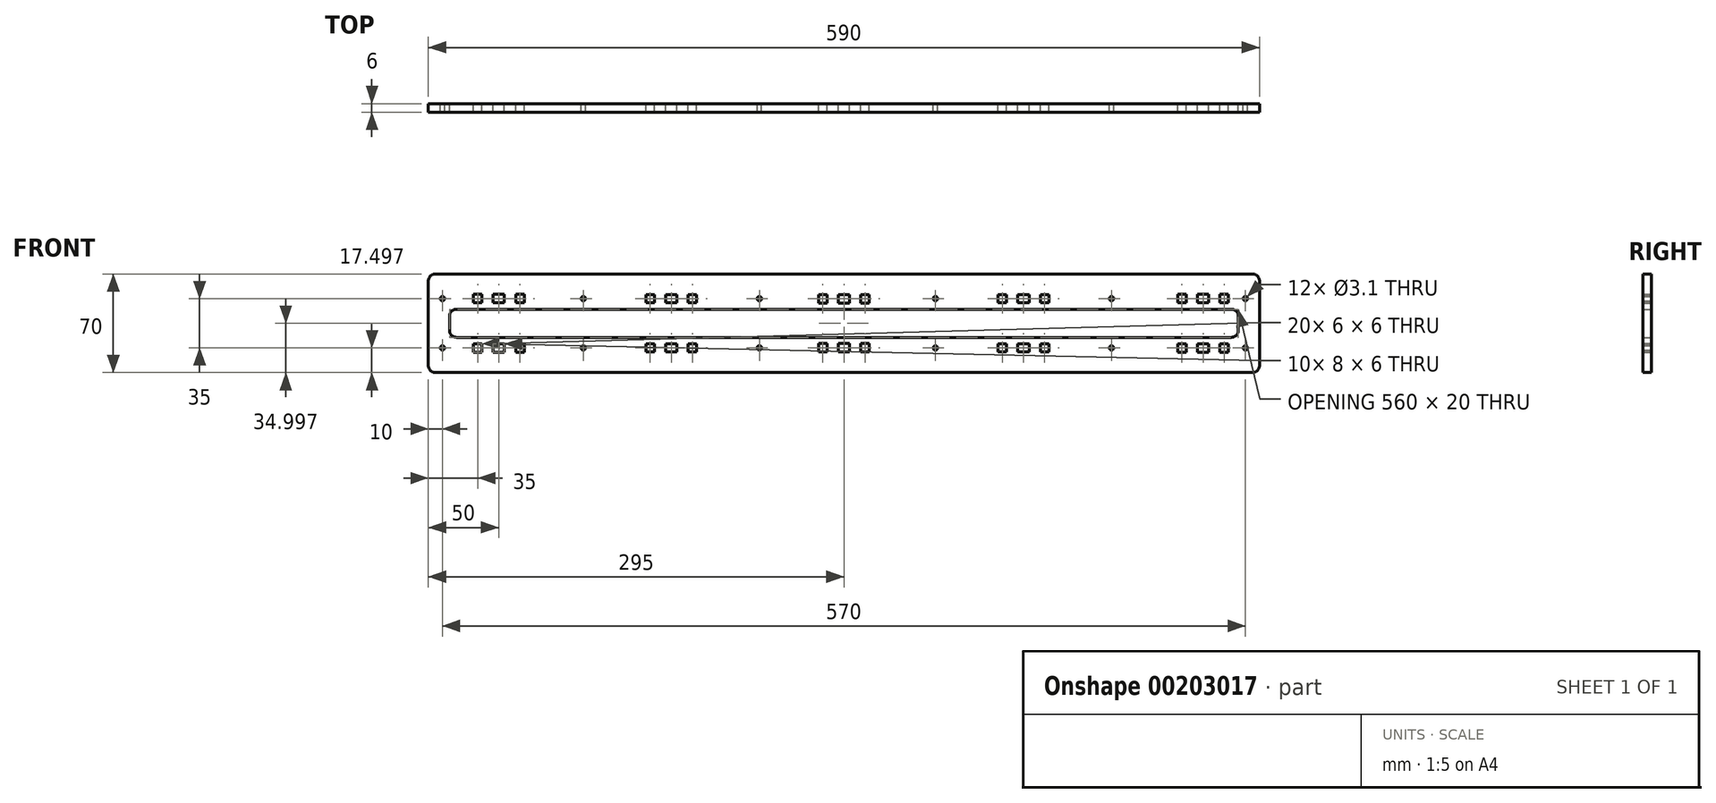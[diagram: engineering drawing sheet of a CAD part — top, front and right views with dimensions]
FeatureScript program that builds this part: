
annotation { "Feature Type Name" : "Feature", "Feature Type Description" : "" }
export const myFeature = defineFeature(function(context is Context, id is Id, definition is map)
    precondition{}
    {
        {
            var Q0;
            Q0=qCreatedBy(makeId("Front.planeOp"),FACE);
            var sketch = newSketch(context, id + "F0", { "sketchPlane" : qUnion([Q0])});
            skLineSegment(sketch, "E0", {"start": v(-295, -83) * mm, "end": v(-295, -23) * mm});
            skArc(sketch, "E1", {"start": v(-295, -23) * mm, "mid": v(-293.54, -19.47) * mm, "end": v(-290, -18) * mm});
            skLineSegment(sketch, "E2", {"start": v(-290, -18) * mm, "end": v(290, -18) * mm});
            skArc(sketch, "E3", {"start": v(290, -18) * mm, "mid": v(293.54, -19.47) * mm, "end": v(295, -23) * mm});
            skLineSegment(sketch, "E4", {"start": v(295, -23) * mm, "end": v(295, -83) * mm});
            skArc(sketch, "E5", {"start": v(295, -83) * mm, "mid": v(293.54, -86.54) * mm, "end": v(290, -88) * mm});
            skLineSegment(sketch, "E6", {"start": v(290, -88) * mm, "end": v(-290, -88) * mm});
            skArc(sketch, "E7", {"start": v(-290, -88) * mm, "mid": v(-293.54, -86.54) * mm, "end": v(-295, -83) * mm});
            skCircle(sketch, "E8", {"center": v(-285, -70.5) * mm, "radius": 1.55 * mm});
            skCircle(sketch, "E9", {"center": v(-285, -35.5) * mm, "radius": 1.55 * mm});
            skCircle(sketch, "E10", {"center": v(285, -70.5) * mm, "radius": 1.55 * mm});
            skCircle(sketch, "E11", {"center": v(285, -35.5) * mm, "radius": 1.55 * mm});
            skLineSegment(sketch, "E12", {"start": v(-275, -43) * mm, "end": v(275, -43) * mm});
            skArc(sketch, "E13", {"start": v(275, -43) * mm, "mid": v(278.54, -44.47) * mm, "end": v(280, -48) * mm});
            skLineSegment(sketch, "E14", {"start": v(280, -48) * mm, "end": v(280, -58) * mm});
            skArc(sketch, "E15", {"start": v(280, -58) * mm, "mid": v(278.54, -61.54) * mm, "end": v(275, -63) * mm});
            skLineSegment(sketch, "E16", {"start": v(275, -63) * mm, "end": v(-275, -63) * mm});
            skArc(sketch, "E17", {"start": v(-275, -63) * mm, "mid": v(-278.54, -61.54) * mm, "end": v(-280, -58) * mm});
            skLineSegment(sketch, "E18", {"start": v(-280, -58) * mm, "end": v(-280, -48) * mm});
            skArc(sketch, "E19", {"start": v(-280, -48) * mm, "mid": v(-278.54, -44.47) * mm, "end": v(-275, -43) * mm});
            skLineSegment(sketch, "E20", {"start": v(-249, -38.5) * mm, "end": v(-249, -32.5) * mm});
            skLineSegment(sketch, "E21", {"start": v(-249, -32.5) * mm, "end": v(-241, -32.5) * mm});
            skLineSegment(sketch, "E22", {"start": v(-241, -32.5) * mm, "end": v(-241, -38.5) * mm});
            skLineSegment(sketch, "E23", {"start": v(-241, -38.5) * mm, "end": v(-249, -38.5) * mm});
            skLineSegment(sketch, "E24", {"start": v(-233, -38.5) * mm, "end": v(-233, -32.5) * mm});
            skLineSegment(sketch, "E25", {"start": v(-233, -32.5) * mm, "end": v(-227, -32.5) * mm});
            skLineSegment(sketch, "E26", {"start": v(-227, -32.5) * mm, "end": v(-227, -38.5) * mm});
            skLineSegment(sketch, "E27", {"start": v(-227, -38.5) * mm, "end": v(-233, -38.5) * mm});
            skLineSegment(sketch, "E28", {"start": v(-257, -38.5) * mm, "end": v(-257, -32.5) * mm});
            skLineSegment(sketch, "E29", {"start": v(-257, -32.5) * mm, "end": v(-263, -32.5) * mm});
            skLineSegment(sketch, "E30", {"start": v(-263, -32.5) * mm, "end": v(-263, -38.5) * mm});
            skLineSegment(sketch, "E31", {"start": v(-263, -38.5) * mm, "end": v(-257, -38.5) * mm});
            skLineSegment(sketch, "E32", {"start": v(-126.5, -38.54) * mm, "end": v(-126.5, -32.54) * mm});
            skLineSegment(sketch, "E33", {"start": v(-126.5, -32.54) * mm, "end": v(-118.5, -32.54) * mm});
            skLineSegment(sketch, "E34", {"start": v(-118.5, -32.54) * mm, "end": v(-118.5, -38.54) * mm});
            skLineSegment(sketch, "E35", {"start": v(-118.5, -38.54) * mm, "end": v(-126.5, -38.54) * mm});
            skLineSegment(sketch, "E36", {"start": v(-110.5, -38.54) * mm, "end": v(-110.5, -32.54) * mm});
            skLineSegment(sketch, "E37", {"start": v(-110.5, -32.54) * mm, "end": v(-104.5, -32.54) * mm});
            skLineSegment(sketch, "E38", {"start": v(-104.5, -32.54) * mm, "end": v(-104.5, -38.54) * mm});
            skLineSegment(sketch, "E39", {"start": v(-104.5, -38.54) * mm, "end": v(-110.5, -38.54) * mm});
            skLineSegment(sketch, "E40", {"start": v(-134.5, -38.54) * mm, "end": v(-134.5, -32.54) * mm});
            skLineSegment(sketch, "E41", {"start": v(-134.5, -32.54) * mm, "end": v(-140.5, -32.54) * mm});
            skLineSegment(sketch, "E42", {"start": v(-140.5, -32.54) * mm, "end": v(-140.5, -38.54) * mm});
            skLineSegment(sketch, "E43", {"start": v(-140.5, -38.54) * mm, "end": v(-134.5, -38.54) * mm});
            skLineSegment(sketch, "E44", {"start": v(-4, -38.57) * mm, "end": v(-4, -32.57) * mm});
            skLineSegment(sketch, "E45", {"start": v(-4, -32.57) * mm, "end": v(4, -32.57) * mm});
            skLineSegment(sketch, "E46", {"start": v(4, -32.57) * mm, "end": v(4, -38.57) * mm});
            skLineSegment(sketch, "E47", {"start": v(4, -38.57) * mm, "end": v(-4, -38.57) * mm});
            skLineSegment(sketch, "E48", {"start": v(12, -38.57) * mm, "end": v(12, -32.57) * mm});
            skLineSegment(sketch, "E49", {"start": v(12, -32.57) * mm, "end": v(18, -32.57) * mm});
            skLineSegment(sketch, "E50", {"start": v(18, -32.57) * mm, "end": v(18, -38.57) * mm});
            skLineSegment(sketch, "E51", {"start": v(18, -38.57) * mm, "end": v(12, -38.57) * mm});
            skLineSegment(sketch, "E52", {"start": v(-12, -38.57) * mm, "end": v(-12, -32.57) * mm});
            skLineSegment(sketch, "E53", {"start": v(-12, -32.57) * mm, "end": v(-18, -32.57) * mm});
            skLineSegment(sketch, "E54", {"start": v(-18, -32.57) * mm, "end": v(-18, -38.57) * mm});
            skLineSegment(sketch, "E55", {"start": v(-18, -38.57) * mm, "end": v(-12, -38.57) * mm});
            skLineSegment(sketch, "E56", {"start": v(123.5, -38.54) * mm, "end": v(123.5, -32.54) * mm});
            skLineSegment(sketch, "E57", {"start": v(123.5, -32.54) * mm, "end": v(131.5, -32.54) * mm});
            skLineSegment(sketch, "E58", {"start": v(131.5, -32.54) * mm, "end": v(131.5, -38.54) * mm});
            skLineSegment(sketch, "E59", {"start": v(131.5, -38.54) * mm, "end": v(123.5, -38.54) * mm});
            skLineSegment(sketch, "E60", {"start": v(139.5, -38.54) * mm, "end": v(139.5, -32.54) * mm});
            skLineSegment(sketch, "E61", {"start": v(139.5, -32.54) * mm, "end": v(145.5, -32.54) * mm});
            skLineSegment(sketch, "E62", {"start": v(145.5, -32.54) * mm, "end": v(145.5, -38.54) * mm});
            skLineSegment(sketch, "E63", {"start": v(145.5, -38.54) * mm, "end": v(139.5, -38.54) * mm});
            skLineSegment(sketch, "E64", {"start": v(115.5, -38.54) * mm, "end": v(115.5, -32.54) * mm});
            skLineSegment(sketch, "E65", {"start": v(115.5, -32.54) * mm, "end": v(109.5, -32.54) * mm});
            skLineSegment(sketch, "E66", {"start": v(109.5, -32.54) * mm, "end": v(109.5, -38.54) * mm});
            skLineSegment(sketch, "E67", {"start": v(109.5, -38.54) * mm, "end": v(115.5, -38.54) * mm});
            skLineSegment(sketch, "E68", {"start": v(251, -38.5) * mm, "end": v(251, -32.5) * mm});
            skLineSegment(sketch, "E69", {"start": v(251, -32.5) * mm, "end": v(259, -32.5) * mm});
            skLineSegment(sketch, "E70", {"start": v(259, -32.5) * mm, "end": v(259, -38.5) * mm});
            skLineSegment(sketch, "E71", {"start": v(259, -38.5) * mm, "end": v(251, -38.5) * mm});
            skLineSegment(sketch, "E72", {"start": v(267, -38.5) * mm, "end": v(267, -32.5) * mm});
            skLineSegment(sketch, "E73", {"start": v(267, -32.5) * mm, "end": v(273, -32.5) * mm});
            skLineSegment(sketch, "E74", {"start": v(273, -32.5) * mm, "end": v(273, -38.5) * mm});
            skLineSegment(sketch, "E75", {"start": v(273, -38.5) * mm, "end": v(267, -38.5) * mm});
            skLineSegment(sketch, "E76", {"start": v(243, -38.5) * mm, "end": v(243, -32.5) * mm});
            skLineSegment(sketch, "E77", {"start": v(243, -32.5) * mm, "end": v(237, -32.5) * mm});
            skLineSegment(sketch, "E78", {"start": v(237, -32.5) * mm, "end": v(237, -38.5) * mm});
            skLineSegment(sketch, "E79", {"start": v(237, -38.5) * mm, "end": v(243, -38.5) * mm});
            skLineSegment(sketch, "E80", {"start": v(-249, -67.5) * mm, "end": v(-249, -73.5) * mm});
            skLineSegment(sketch, "E81", {"start": v(-249, -73.5) * mm, "end": v(-241, -73.5) * mm});
            skLineSegment(sketch, "E82", {"start": v(-241, -73.5) * mm, "end": v(-241, -67.5) * mm});
            skLineSegment(sketch, "E83", {"start": v(-241, -67.5) * mm, "end": v(-249, -67.5) * mm});
            skLineSegment(sketch, "E84", {"start": v(-233, -67.5) * mm, "end": v(-233, -73.5) * mm});
            skLineSegment(sketch, "E85", {"start": v(-233, -73.5) * mm, "end": v(-227, -73.5) * mm});
            skLineSegment(sketch, "E86", {"start": v(-227, -73.5) * mm, "end": v(-227, -67.5) * mm});
            skLineSegment(sketch, "E87", {"start": v(-227, -67.5) * mm, "end": v(-233, -67.5) * mm});
            skLineSegment(sketch, "E88", {"start": v(-257, -67.5) * mm, "end": v(-257, -73.5) * mm});
            skLineSegment(sketch, "E89", {"start": v(-257, -73.5) * mm, "end": v(-263, -73.5) * mm});
            skLineSegment(sketch, "E90", {"start": v(-263, -73.5) * mm, "end": v(-263, -67.5) * mm});
            skLineSegment(sketch, "E91", {"start": v(-263, -67.5) * mm, "end": v(-257, -67.5) * mm});
            skLineSegment(sketch, "E92", {"start": v(-126.5, -67.47) * mm, "end": v(-126.5, -73.47) * mm});
            skLineSegment(sketch, "E93", {"start": v(-126.5, -73.47) * mm, "end": v(-118.5, -73.47) * mm});
            skLineSegment(sketch, "E94", {"start": v(-118.5, -73.47) * mm, "end": v(-118.5, -67.47) * mm});
            skLineSegment(sketch, "E95", {"start": v(-118.5, -67.47) * mm, "end": v(-126.5, -67.47) * mm});
            skLineSegment(sketch, "E96", {"start": v(-110.5, -67.47) * mm, "end": v(-110.5, -73.47) * mm});
            skLineSegment(sketch, "E97", {"start": v(-110.5, -73.47) * mm, "end": v(-104.5, -73.47) * mm});
            skLineSegment(sketch, "E98", {"start": v(-104.5, -73.47) * mm, "end": v(-104.5, -67.47) * mm});
            skLineSegment(sketch, "E99", {"start": v(-104.5, -67.47) * mm, "end": v(-110.5, -67.47) * mm});
            skLineSegment(sketch, "E100", {"start": v(-134.5, -67.47) * mm, "end": v(-134.5, -73.47) * mm});
            skLineSegment(sketch, "E101", {"start": v(-134.5, -73.47) * mm, "end": v(-140.5, -73.47) * mm});
            skLineSegment(sketch, "E102", {"start": v(-140.5, -73.47) * mm, "end": v(-140.5, -67.47) * mm});
            skLineSegment(sketch, "E103", {"start": v(-140.5, -67.47) * mm, "end": v(-134.5, -67.47) * mm});
            skLineSegment(sketch, "E104", {"start": v(-4, -67.43) * mm, "end": v(-4, -73.43) * mm});
            skLineSegment(sketch, "E105", {"start": v(-4, -73.43) * mm, "end": v(4, -73.43) * mm});
            skLineSegment(sketch, "E106", {"start": v(4, -73.43) * mm, "end": v(4, -67.43) * mm});
            skLineSegment(sketch, "E107", {"start": v(4, -67.43) * mm, "end": v(-4, -67.43) * mm});
            skLineSegment(sketch, "E108", {"start": v(12, -67.43) * mm, "end": v(12, -73.43) * mm});
            skLineSegment(sketch, "E109", {"start": v(12, -73.43) * mm, "end": v(18, -73.43) * mm});
            skLineSegment(sketch, "E110", {"start": v(18, -73.43) * mm, "end": v(18, -67.43) * mm});
            skLineSegment(sketch, "E111", {"start": v(18, -67.43) * mm, "end": v(12, -67.43) * mm});
            skLineSegment(sketch, "E112", {"start": v(-12, -67.43) * mm, "end": v(-12, -73.43) * mm});
            skLineSegment(sketch, "E113", {"start": v(-12, -73.43) * mm, "end": v(-18, -73.43) * mm});
            skLineSegment(sketch, "E114", {"start": v(-18, -73.43) * mm, "end": v(-18, -67.43) * mm});
            skLineSegment(sketch, "E115", {"start": v(-18, -67.43) * mm, "end": v(-12, -67.43) * mm});
            skLineSegment(sketch, "E116", {"start": v(123.5, -67.47) * mm, "end": v(123.5, -73.47) * mm});
            skLineSegment(sketch, "E117", {"start": v(123.5, -73.47) * mm, "end": v(131.5, -73.47) * mm});
            skLineSegment(sketch, "E118", {"start": v(131.5, -73.47) * mm, "end": v(131.5, -67.47) * mm});
            skLineSegment(sketch, "E119", {"start": v(131.5, -67.47) * mm, "end": v(123.5, -67.47) * mm});
            skLineSegment(sketch, "E120", {"start": v(139.5, -67.47) * mm, "end": v(139.5, -73.47) * mm});
            skLineSegment(sketch, "E121", {"start": v(139.5, -73.47) * mm, "end": v(145.5, -73.47) * mm});
            skLineSegment(sketch, "E122", {"start": v(145.5, -73.47) * mm, "end": v(145.5, -67.47) * mm});
            skLineSegment(sketch, "E123", {"start": v(145.5, -67.47) * mm, "end": v(139.5, -67.47) * mm});
            skLineSegment(sketch, "E124", {"start": v(115.5, -67.47) * mm, "end": v(115.5, -73.47) * mm});
            skLineSegment(sketch, "E125", {"start": v(115.5, -73.47) * mm, "end": v(109.5, -73.47) * mm});
            skLineSegment(sketch, "E126", {"start": v(109.5, -73.47) * mm, "end": v(109.5, -67.47) * mm});
            skLineSegment(sketch, "E127", {"start": v(109.5, -67.47) * mm, "end": v(115.5, -67.47) * mm});
            skLineSegment(sketch, "E128", {"start": v(251, -67.5) * mm, "end": v(251, -73.5) * mm});
            skLineSegment(sketch, "E129", {"start": v(251, -73.5) * mm, "end": v(259, -73.5) * mm});
            skLineSegment(sketch, "E130", {"start": v(259, -73.5) * mm, "end": v(259, -67.5) * mm});
            skLineSegment(sketch, "E131", {"start": v(259, -67.5) * mm, "end": v(251, -67.5) * mm});
            skLineSegment(sketch, "E132", {"start": v(267, -67.5) * mm, "end": v(267, -73.5) * mm});
            skLineSegment(sketch, "E133", {"start": v(267, -73.5) * mm, "end": v(273, -73.5) * mm});
            skLineSegment(sketch, "E134", {"start": v(273, -73.5) * mm, "end": v(273, -67.5) * mm});
            skLineSegment(sketch, "E135", {"start": v(273, -67.5) * mm, "end": v(267, -67.5) * mm});
            skLineSegment(sketch, "E136", {"start": v(243, -67.5) * mm, "end": v(243, -73.5) * mm});
            skLineSegment(sketch, "E137", {"start": v(243, -73.5) * mm, "end": v(237, -73.5) * mm});
            skLineSegment(sketch, "E138", {"start": v(237, -73.5) * mm, "end": v(237, -67.5) * mm});
            skLineSegment(sketch, "E139", {"start": v(237, -67.5) * mm, "end": v(243, -67.5) * mm});
            skCircle(sketch, "E140", {"center": v(-185, -70.5) * mm, "radius": 1.55 * mm});
            skCircle(sketch, "E141", {"center": v(-185, -35.5) * mm, "radius": 1.55 * mm});
            skCircle(sketch, "E142", {"center": v(-60, -70.5) * mm, "radius": 1.55 * mm});
            skCircle(sketch, "E143", {"center": v(-60, -35.5) * mm, "radius": 1.55 * mm});
            skCircle(sketch, "E144", {"center": v(65, -70.5) * mm, "radius": 1.55 * mm});
            skCircle(sketch, "E145", {"center": v(65, -35.5) * mm, "radius": 1.55 * mm});
            skCircle(sketch, "E146", {"center": v(190, -70.5) * mm, "radius": 1.55 * mm});
            skCircle(sketch, "E147", {"center": v(190, -35.5) * mm, "radius": 1.55 * mm});
            skSolve(sketch);
        }
        {
            var Q0;
            Q0=makeQuery(id+"F0.imprint","IMPRINT",FACE,{"disambiguationData":[TD([[makeQuery(id+"F0.imprint","IMPRINT",EDGE,{"derivedFrom":sQuery(id+"F0.wireOp",EDGE,"E0")}),-1.0]])]});
            extrude(context, id + "F1", {"entities" : qUnion([Q0]), "depth" : 6 * mm});
        }
    });
